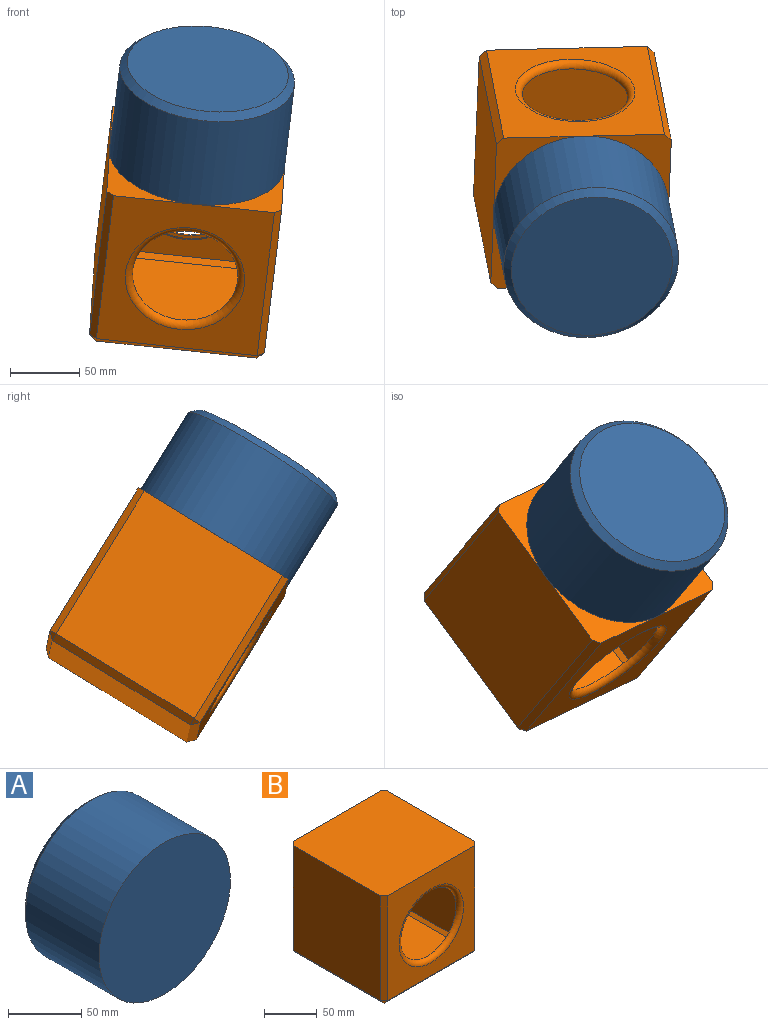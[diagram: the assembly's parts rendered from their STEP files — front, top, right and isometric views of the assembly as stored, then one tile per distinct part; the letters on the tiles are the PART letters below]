
ASSEMBLY  parts=2 mates=1
PART A: 4 faces, bbox 127x76.2x127 mm
  f0: cylinder r=63.5mm len=127mm, axis (0,1,0), area 28375.6mm2, adj f1,f3
  f1: plane 127x127mm, normal (0,-1,0), area 12667.7mm2, adj f0
  f2: plane 116.84x116.84mm, normal (0,1,0), area 10721.9mm2, adj f3
  f3: cone r=63.5mm half-angle=45deg, axis (0,-1,0), area 2751.7mm2, adj f0,f2
PART B: 42 faces, bbox 127x127x127 mm
  f0: plane 121.92x116.84mm, normal (-1,0,0), area 14245.1mm2, adj f3,f8,f13,f14
  f1: plane 116.84x116.84mm, normal (0,0,-1), area 13651.6mm2, adj f10,f13,f16,f19
  f2: plane 121.92x116.84mm, normal (1,0,0), area 14245.1mm2, adj f3,f9,f15,f16
  f3: plane 127x127mm, normal (0,0,1), area 16077.4mm2, adj f0,f2,f4,f5,f8,f9,f14,f15
  f4: plane 121.92x116.84mm, normal (0,-1,0), area 8387.6mm2, adj f3,f7,f14,f15,f19
  f5: plane 121.92x116.84mm, normal (0,1,0), area 8387.6mm2, adj f3,f6,f8,f9,f10
  f6: torus R=43.18mm, axis (0,-1,0), area 2002.8mm2, adj f5,f21
  f7: torus R=43.18mm, axis (0,-1,0), area 2002.8mm2, adj f4,f20
  f8: plane 121.92x5.08mm, normal (-0.71,0.71,0), area 875.9mm2, adj f0,f3,f5,f11
  f9: plane 121.92x5.08mm, normal (0.71,0.71,0), area 875.9mm2, adj f2,f3,f5,f12
  f10: plane 116.84x5.08mm, normal (0,0.71,-0.71), area 839.4mm2, adj f1,f5,f11,f12
  f11: plane 5.08x5.08mm, normal (-0.58,0.58,-0.58), area 22.3mm2, adj f8,f10,f13
  f12: plane 5.08x5.08mm, normal (0.58,0.58,-0.58), area 22.3mm2, adj f9,f10,f16
  f13: plane 116.84x5.08mm, normal (-0.71,0,-0.71), area 839.4mm2, adj f0,f1,f11,f17
  f14: plane 121.92x5.08mm, normal (-0.71,-0.71,0), area 875.9mm2, adj f0,f3,f4,f17
  f15: plane 121.92x5.08mm, normal (0.71,-0.71,0), area 875.9mm2, adj f2,f3,f4,f18
  f16: plane 116.84x5.08mm, normal (0.71,0,-0.71), area 839.4mm2, adj f1,f2,f12,f18
  f17: plane 5.08x5.08mm, normal (-0.58,-0.58,-0.58), area 22.3mm2, adj f13,f14,f19
  f18: plane 5.08x5.08mm, normal (0.58,-0.58,-0.58), area 22.3mm2, adj f15,f16,f19
  f19: plane 116.84x5.08mm, normal (0,-0.71,-0.71), area 839.4mm2, adj f1,f4,f17,f18
  f20: plane 81.28x81.28mm, normal (0,1,0), area 628.3mm2, adj f7,f29
  f21: plane 81.28x81.28mm, normal (0,-1,0), area 628.3mm2, adj f6,f28
  f22: plane 118.33x114.74mm, normal (1,0,0), area 13576.4mm2, adj f25,f30,f35,f36
  f23: plane 114.74x114.74mm, normal (0,0,1), area 13164.3mm2, adj f32,f35,f38,f41
  f24: plane 118.33x114.74mm, normal (-1,0,0), area 13576.4mm2, adj f25,f31,f37,f38
  f25: plane 121.92x121.92mm, normal (0,0,-1), area 14838.7mm2, adj f22,f24,f26,f27,f30,f31,f36,f37
  f26: plane 118.33x114.74mm, normal (0,1,0), area 7718.9mm2, adj f25,f29,f36,f37,f41
  f27: plane 118.33x114.74mm, normal (0,-1,0), area 7718.9mm2, adj f25,f28,f30,f31,f32
  f28: torus R=43.18mm, axis (0,-1,0), area 1041.9mm2, adj f21,f27
  f29: torus R=43.18mm, axis (0,-1,0), area 1041.9mm2, adj f20,f26
  f30: plane 118.57x3.59mm, normal (0.71,-0.71,0), area 602.3mm2, adj f22,f25,f27,f32,f33,f35
  f31: plane 118.57x3.59mm, normal (-0.71,-0.71,0), area 602.3mm2, adj f24,f25,f27,f32,f34,f38
  f32: plane 115.23x3.59mm, normal (0,-0.71,0.71), area 585.2mm2, adj f23,f27,f30,f31,f33,f34,f35,f38
  f33: plane 3.1x3.1mm, normal (0.58,-0.58,0.58), area 8.3mm2, adj f30,f32,f35
  f34: plane 3.1x3.1mm, normal (-0.58,-0.58,0.58), area 8.3mm2, adj f31,f32,f38
  f35: plane 115.23x3.59mm, normal (0.71,0,0.71), area 585.2mm2, adj f22,f23,f30,f32,f33,f36,f39,f41
  f36: plane 118.57x3.59mm, normal (0.71,0.71,0), area 602.3mm2, adj f22,f25,f26,f35,f39,f41
  f37: plane 118.57x3.59mm, normal (-0.71,0.71,0), area 602.3mm2, adj f24,f25,f26,f38,f40,f41
  f38: plane 115.23x3.59mm, normal (-0.71,0,0.71), area 585.2mm2, adj f23,f24,f31,f32,f34,f37,f40,f41
  f39: plane 3.1x3.1mm, normal (0.58,0.58,0.58), area 8.3mm2, adj f35,f36,f41
  f40: plane 3.1x3.1mm, normal (-0.58,0.58,0.58), area 8.3mm2, adj f37,f38,f41
  f41: plane 115.23x3.59mm, normal (0,0.71,0.71), area 585.2mm2, adj f23,f26,f35,f36,f37,f38,f39,f40
PLACE A rot(axis=(1,0.04,-0.05),121.6deg) t=(79.15,-148.05,293.2)mm
PLACE B rot(axis=(0.98,0.19,-0.01),32.1deg) t=(-2.49,10.67,160.92)mm
MATE fastened B.f3 <-> A.f0  axis (0.1,-0.52,0.85) through (71.37,-108.28,228.67)mm
